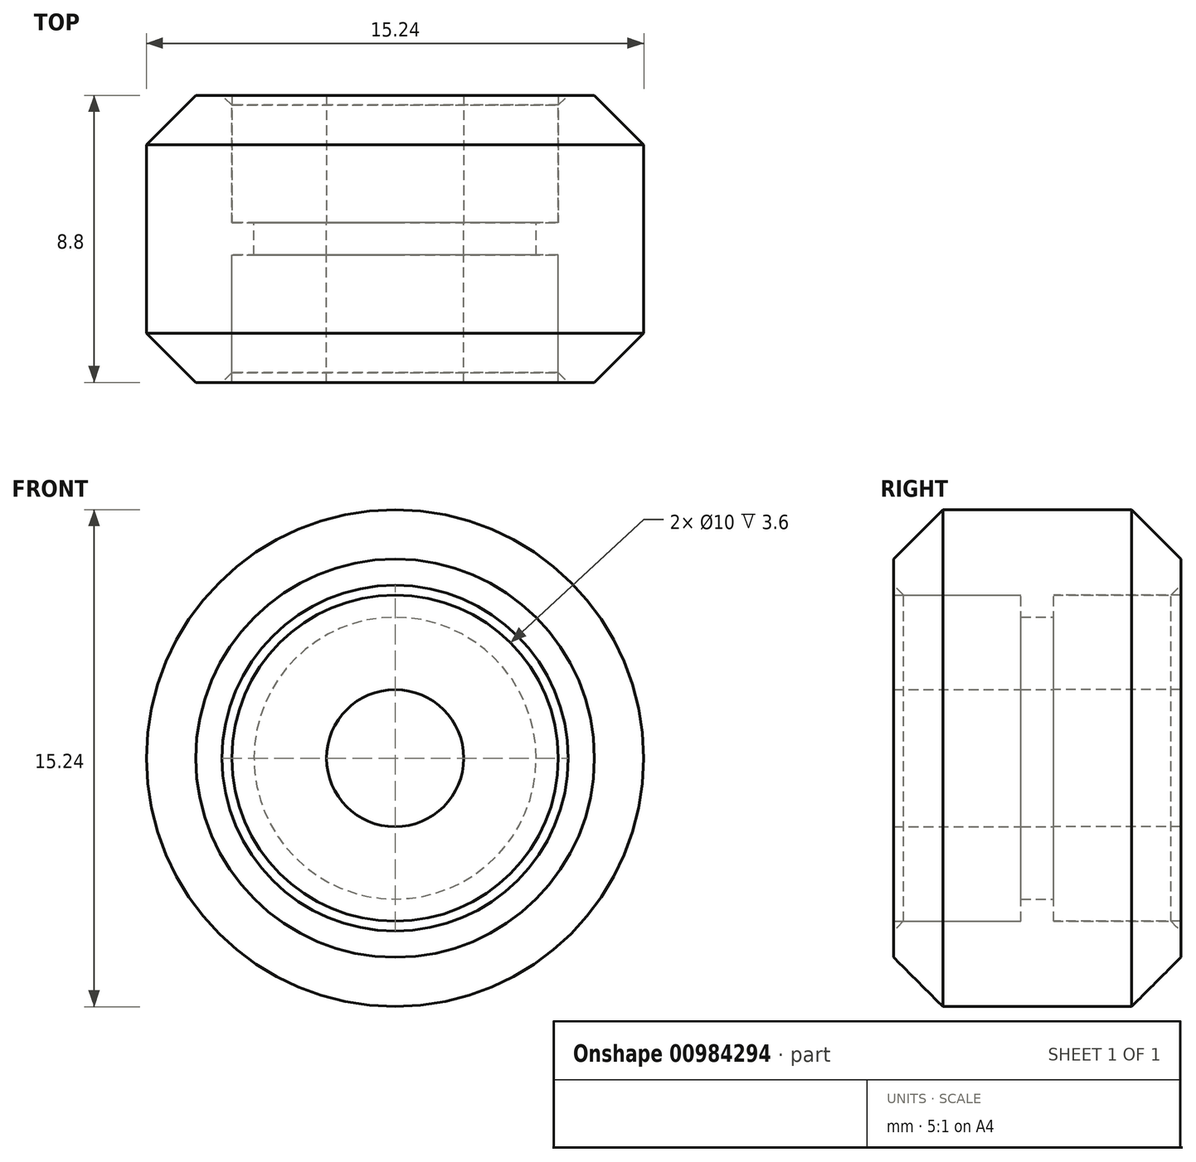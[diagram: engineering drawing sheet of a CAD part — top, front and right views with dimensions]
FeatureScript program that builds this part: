
annotation { "Feature Type Name" : "Feature", "Feature Type Description" : "" }
export const myFeature = defineFeature(function(context is Context, id is Id, definition is map)
    precondition{}
    {
        {
            var Q0;
            Q0=qCreatedBy(makeId("Front.planeOp"),FACE);
            var sketch = newSketch(context, id + "F0", { "sketchPlane" : qUnion([Q0])});
            skCircle(sketch, "E0", {"center": v(0, 0) * mm, "radius": 7.62 * mm});
            skCircle(sketch, "E1", {"center": v(0, 0) * mm, "radius": 5 * mm});
            skCircle(sketch, "E2", {"center": v(0, 0) * mm, "radius": 4.32 * mm});
            skCircle(sketch, "E3", {"center": v(0, 0) * mm, "radius": 2.1 * mm});
            skSolve(sketch);
        }
        {
            var Q0;
            Q0=makeQuery(id+"F0.imprint","IMPRINT",FACE,{"disambiguationData":[TD([[makeQuery(id+"F0.imprint","IMPRINT",EDGE,{"derivedFrom":sQuery(id+"F0.wireOp",EDGE,"E0")}),1.0]])]});
            extrude(context, id + "F1", {"entities" : qUnion([Q0]), "depth" : 4.4 * mm, "offsetDistance" : 25 * mm, "hasSecondDirection" : true, "secondDirectionOppositeDirection" : true, "secondDirectionDepth" : 4.4 * mm});
        }
        {
            var Q0;
            Q0=makeQuery(id+"F0.imprint","IMPRINT",FACE,{"disambiguationData":[TD([[makeQuery(id+"F0.imprint","IMPRINT",EDGE,{"derivedFrom":sQuery(id+"F0.wireOp",EDGE,"E1")}),1.0]])]});
            extrude(context, id + "F2", {"entities" : qUnion([Q0]), "operationType" : NewBodyOperationType.ADD, "depth" : 0.5 * mm, "offsetDistance" : 25 * mm, "hasSecondDirection" : true, "secondDirectionOppositeDirection" : true, "secondDirectionDepth" : 0.5 * mm});
        }
        {
            var Q0;
            Q0=makeQuery(id+"F1.opExtrude","CAP_EDGE",EDGE,{"disambiguationData":[OSD([sQuery(id+"F0.wireOp",EDGE,"E0")])],"isStart":true});
            var Q1;
            Q1=makeQuery(id+"F1.opExtrude","CAP_EDGE",EDGE,{"disambiguationData":[OSD([sQuery(id+"F0.wireOp",EDGE,"E0")])],"isStart":false});
            chamfer(context, id + "F3", {"entities" : qUnion([Q0, Q1]), "width" : 1.51 * mm, "tangentPropagation" : true});
        }
        {
            var Q0;
            Q0=makeQuery(id+"F1.opExtrude","CAP_EDGE",EDGE,{"disambiguationData":[OSD([sQuery(id+"F0.wireOp",EDGE,"E1")])],"isStart":false});
            var Q1;
            Q1=makeQuery(id+"F1.opExtrude","CAP_EDGE",EDGE,{"disambiguationData":[OSD([sQuery(id+"F0.wireOp",EDGE,"E1")])],"isStart":true});
            chamfer(context, id + "F4", {"entities" : qUnion([Q0, Q1]), "width" : 0.3 * mm, "tangentPropagation" : true});
        }
        {
            var Q0;
            Q0=makeQuery(id+"F0.imprint","IMPRINT",FACE,{"disambiguationData":[TD([[makeQuery(id+"F0.imprint","IMPRINT",EDGE,{"derivedFrom":sQuery(id+"F0.wireOp",EDGE,"E2")}),1.0]])]});
            var Q1;
            Q1=makeQuery(id+"F0.imprint","IMPRINT",FACE,{"disambiguationData":[TD([[makeQuery(id+"F0.imprint","IMPRINT",EDGE,{"derivedFrom":sQuery(id+"F0.wireOp",EDGE,"E1")}),1.0]])]});
            extrude(context, id + "F5", {"entities" : qUnion([Q0, Q1]), "depth" : 4.4 * mm, "offsetDistance" : 25 * mm, "hasSecondDirection" : true, "secondDirectionOppositeDirection" : false, "secondDirectionDepth" : 0.5 * mm});
        }
        {
            var Q0;
            Q0=makeQuery(id+"F0.imprint","IMPRINT",FACE,{"disambiguationData":[TD([[makeQuery(id+"F0.imprint","IMPRINT",EDGE,{"derivedFrom":sQuery(id+"F0.wireOp",EDGE,"E2")}),1.0]])]});
            var Q1;
            Q1=makeQuery(id+"F0.imprint","IMPRINT",FACE,{"disambiguationData":[TD([[makeQuery(id+"F0.imprint","IMPRINT",EDGE,{"derivedFrom":sQuery(id+"F0.wireOp",EDGE,"E1")}),1.0]])]});
            extrude(context, id + "F6", {"entities" : qUnion([Q0, Q1]), "oppositeDirection" : true, "depth" : 4.4 * mm, "offsetDistance" : 25 * mm, "hasSecondDirection" : true, "secondDirectionOppositeDirection" : true, "secondDirectionDepth" : 0.5 * mm});
        }
        {
            var Q0;
            Q0=makeQuery(id+"F0.imprint","IMPRINT",FACE,{"disambiguationData":[TD([[makeQuery(id+"F0.imprint","IMPRINT",EDGE,{"derivedFrom":sQuery(id+"F0.wireOp",EDGE,"E2")}),1.0]])]});
            extrude(context, id + "F7", {"entities" : qUnion([Q0]), "depth" : 0.5 * mm, "offsetDistance" : 25 * mm, "hasSecondDirection" : true, "secondDirectionOppositeDirection" : true, "secondDirectionDepth" : 0.5 * mm});
        }
    });
